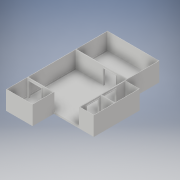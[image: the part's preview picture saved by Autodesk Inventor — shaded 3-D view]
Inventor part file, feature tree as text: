
AUTODESK INVENTOR PART (.ipt)
format: ipt  version: 2017 (Build 210142000, 142)  size: 408,064 bytes
history: native  units: in
note: dims shown in document units (in); Inventor stores cm internally (conversion verified against a paired STEP export)
features: extrude x9, sketch x7, other x2, plane x1
ambient origin geometry x8: Origin, YZ Plane, XZ Plane, XY Plane, X Axis, Y Axis, Z Axis, Center Point
bodies: Solid1 (feature_tree)
feature tree (19):
  extrude  "floor"  Depth=30.5in
  extrude  "walls"  Depth=15.5in
  extrude  "trim"  Depth=11.5in
  extrude  "doorframe 1 and 2"  Depth=14.5in
  extrude  "door frame 3"  Depth=39.0in
  extrude  "door frame 4"  Depth=1.0in TaperAngle=0.0deg
  other  "door trim workplane 1 and 2"
  extrude  "door trim 1 and 2"  Depth=0.25in
  other  "door time workplane 3"
  extrude  "door trim 3"  Depth=0.25in
  plane  "Work Plane3"
  extrude  "door trim 4"  Depth=0.25in
  sketch  "Sketch1"  dims[d0=35.5in d1=30.5in]
  sketch  "Sketch4"  dims[d2=12.5in d3=15.5in]
  sketch  "Sketch5"  dims[d4=12.5in d5=11.5in]
  sketch  "Sketch7"  dims[d6=12.5in d7=14.5in]
  sketch  "Sketch8"  dims[d9=18.5in d11=39.0in]
  sketch  "Sketch9"  dims[d12=30.5in d13=1.0in d14=0.0in]
  sketch  "Sketch10"  dims[d27=12.5in d28=0.25in d30=0.25in d31=0.25in d34=0.25in d38=0.25in d39=0.25in d40=0.25in d41=0.25in d42=0.25in d43=0.25in d44=10.0in d45=0.0in d48=0.25in d49=0.25in d50=0.25in d51=0.25in d52=0.0833in d55=0.0833in d56=0.0833in d57=0.828in d58=0.0in d59=7.5in d60=8.8in d61=1.0in d63=0.5in d64=0.25in d67=38.75in d68=0.0in d69=26.75in d70=0.0833in d71=0.0833in d76=0.0833in d77=0.0833in d78=0.0833in d79=0.0833in d80=0.0833in d81=0.828in d82=0.0in d83=7.5in d84=8.8in d86=10.0in d87=0.828in d88=0.0in d89=7.5in d90=8.8in d91=1.0in d92=0.828in d93=0.0in d94=0.305in d95=0.305in d96=0.305in d97=0.305in d98=0.305in d99=0.305in d100=1.0in d101=0.0in d102=0.305in d103=0.305in d104=0.305in d105=0.305in d106=1.0in d107=0.0in d108=0.305in d109=0.305in d110=0.305in d111=0.305in d112=1.0in d113=0.0in d114=0.25in]
